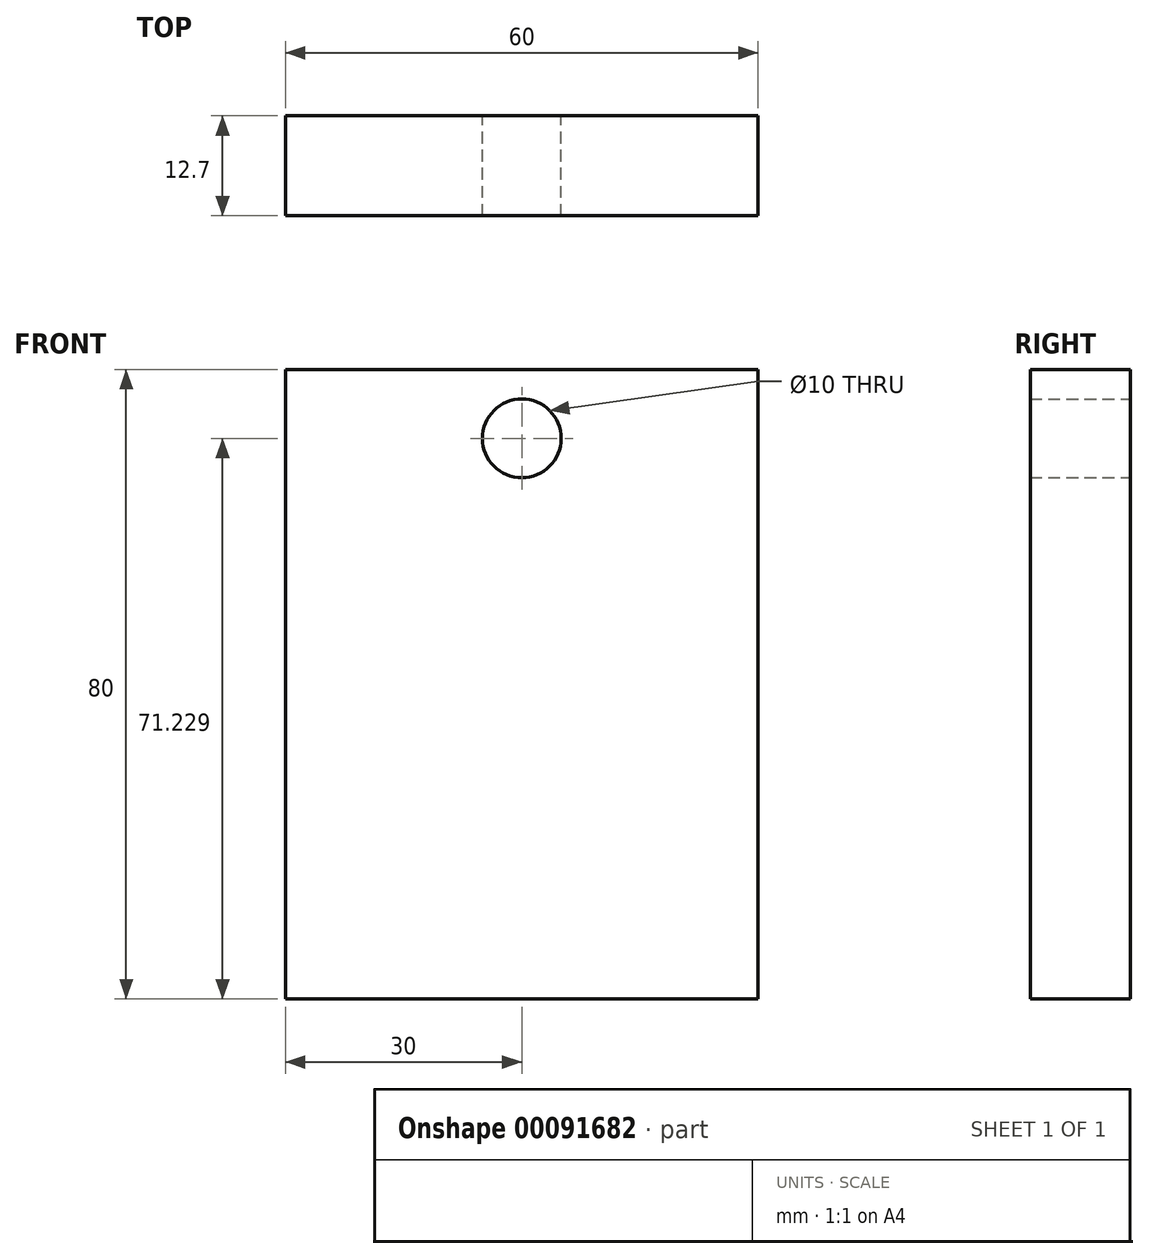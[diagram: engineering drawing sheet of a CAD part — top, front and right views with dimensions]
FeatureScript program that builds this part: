
annotation { "Feature Type Name" : "Feature", "Feature Type Description" : "" }
export const myFeature = defineFeature(function(context is Context, id is Id, definition is map)
    precondition{}
    {
        {
            var Q0;
            Q0=qCreatedBy(makeId("Front.planeOp"),FACE);
            var sketch = newSketch(context, id + "F0", { "sketchPlane" : qUnion([Q0])});
            skLineSegment(sketch, "E0.bottom", {"start": v(-30, 40) * mm, "end": v(30, 40) * mm});
            skLineSegment(sketch, "E0.top", {"start": v(-30, -40) * mm, "end": v(30, -40) * mm});
            skLineSegment(sketch, "E0.left", {"start": v(-30, 40) * mm, "end": v(-30, -40) * mm});
            skLineSegment(sketch, "E0.right", {"start": v(30, 40) * mm, "end": v(30, -40) * mm});
            skPoint(sketch, "E0.middle", {"position": v(0, 0) * mm});
            skCircle(sketch, "E1", {"center": v(0, -16.85) * mm, "radius": 20 * mm});
            skCircle(sketch, "E2", {"center": v(0, 13.35) * mm, "radius": 10 * mm});
            skCircle(sketch, "E3", {"center": v(0, 31.23) * mm, "radius": 5 * mm});
            skSolve(sketch);
        }
        {
            var Q0;
            Q0=makeQuery(id+"F0.imprint","IMPRINT",FACE,{"disambiguationData":[TD([[makeQuery(id+"F0.imprint","IMPRINT",EDGE,{"derivedFrom":sQuery(id+"F0.wireOp",EDGE,"E0.bottom")}),-1.0]])]});
            extrude(context, id + "F1", {"entities" : qUnion([Q0]), "depth" : 6.35 * mm});
        }
        {
            var Q0;
            Q0=makeQuery(id+"F0.imprint","IMPRINT",FACE,{"disambiguationData":[TD([[makeQuery(id+"F0.imprint","IMPRINT",EDGE,{"derivedFrom":sQuery(id+"F0.wireOp",EDGE,"E1")}),1.0]])]});
            var Q1;
            {var subQ0=sQuery(id+"F0.wireOp",EDGE,"E3");var subQ1=sQuery(id+"F0.wireOp",EDGE,"E2");var subQ2=makeQuery(id+"F0.imprint","INTERSECT",VERTEX,{"disambiguationData":[OD(0.0)],"derivedFrom":[subQ1,subQ0]});Q1=makeQuery(id+"F0.imprint","IMPRINT",FACE,{"disambiguationData":[TD([[makeQuery(id+"F0.imprint","IMPRINT",EDGE,{"disambiguationData":[TD([[subQ2,1.0]])],"derivedFrom":subQ1}),1.0]])]});}
            var Q2;
            {var subQ0=sQuery(id+"F0.wireOp",EDGE,"E3");var subQ1=sQuery(id+"F0.wireOp",EDGE,"E2");var subQ2=makeQuery(id+"F0.imprint","INTERSECT",VERTEX,{"disambiguationData":[OD(0.0)],"derivedFrom":[subQ1,subQ0]});Q2=makeQuery(id+"F0.imprint","IMPRINT",FACE,{"disambiguationData":[TD([[makeQuery(id+"F0.imprint","IMPRINT",EDGE,{"disambiguationData":[TD([[subQ2,-1.0]])],"derivedFrom":subQ1}),-1.0]])]});}
            extrude(context, id + "F2", {"entities" : qUnion([Q0, Q1, Q2]), "operationType" : NewBodyOperationType.ADD, "depth" : 12.7 * mm});
        }
    });
